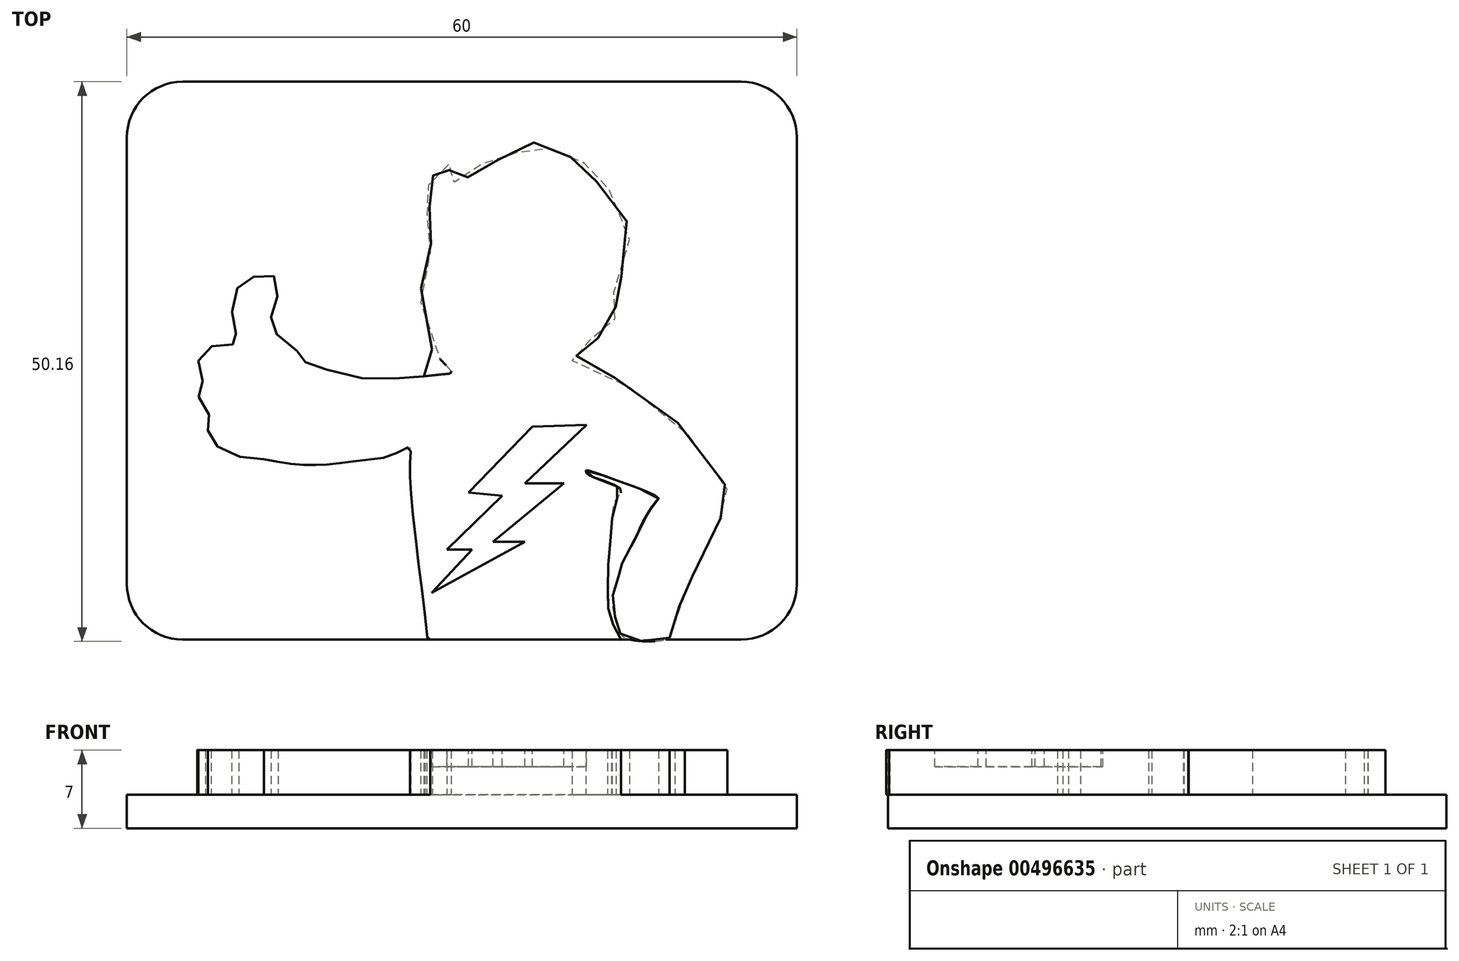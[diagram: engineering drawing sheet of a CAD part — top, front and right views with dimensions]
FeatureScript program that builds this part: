
annotation { "Feature Type Name" : "Feature", "Feature Type Description" : "" }
export const myFeature = defineFeature(function(context is Context, id is Id, definition is map)
    precondition{}
    {
        {
            var Q0;
            Q0=qCreatedBy(makeId("Top.planeOp"),FACE);
            var sketch = newSketch(context, id + "F0", { "sketchPlane" : qUnion([Q0])});
            skLineSegment(sketch, "E0", {"start": v(23.2, 0) * mm, "end": v(40.3, 0) * mm});
            skFitSpline(sketch, "E1", {"points": [v(40.3, 0) * mm, v(39.62, 1.25) * mm, v(39.17, 2.66) * mm, v(39.1, 4.54) * mm, v(39.2, 7.51) * mm, v(39.48, 10.18) * mm, v(39.82, 12.47) * mm, v(40.3, 13.43) * mm, v(37.7, 14.6) * mm, v(37.2, 14.94) * mm, v(37.16, 15.14) * mm, v(38.73, 14.7) * mm, v(43.66, 12.71) * mm, v(43.48, 12.44) * mm, v(42.15, 10.32) * mm, v(41.53, 8.95) * mm, v(40.54, 7.2) * mm, v(40.3, 6.45) * mm, v(39.96, 5.29) * mm, v(39.52, 3.2) * mm, v(40.08, 1.08) * mm, v(40.66, 0.15) * mm, v(44.65, 0.15) * mm, v(44.99, 0.8) * mm, v(45.31, 1.26) * mm, v(45.21, 2.3) * mm, v(44.8, 3.13) * mm, v(44.18, 3.06) * mm, v(43.76, 2.55) * mm, v(43.43, 2.1) * mm, v(43.67, 1.59) * mm, v(44.17, 1.67) * mm, v(44.47, 1.04) * mm, v(44.03, 0.78) * mm, v(43.09, 1.49) * mm, v(43.33, 2.68) * mm, v(43.83, 3.3) * mm, v(43.86, 3.57) * mm, v(42.44, 3.86) * mm, v(41.6, 4.26) * mm, v(41.02, 4.75) * mm, v(40.5, 5.45) * mm, v(39.97, 5.3) * mm], "startDerivative": vector(-28.08, 47.6) * mm, "endDerivative": vector(-35.62, -20.95) * mm});
            skFitSpline(sketch, "E2", {"points": [v(44.65, 0.15) * mm, v(45.37, 0.15) * mm, v(45.62, 0.84) * mm, v(46.02, 1.62) * mm, v(45.65, 2.6) * mm, v(45.25, 3.45) * mm, v(45.12, 3.62) * mm, v(45.53, 4.1) * mm, v(46.27, 4.98) * mm, v(46.55, 5.43) * mm, v(47.25, 6.7) * mm, v(48.46, 9.23) * mm, v(49.19, 10.82) * mm, v(49.4, 11.55) * mm, v(49.65, 12.38) * mm, v(49.8, 12.93) * mm, v(49.82, 13.33) * mm, v(49.73, 13.67) * mm, v(49.09, 14.73) * mm, v(47.87, 16.42) * mm, v(44.79, 20.02) * mm, v(43.5, 20.9) * mm, v(40.2, 23.17) * mm, v(38.18, 24.15) * mm, v(36.07, 24.93) * mm, v(35.93, 25.02) * mm, v(36.04, 25.17) * mm, v(36.55, 25.71) * mm, v(36.82, 26.15) * mm, v(37.2, 26.6) * mm, v(37.4, 26.83) * mm, v(37.58, 26.9) * mm, v(37.85, 26.9) * mm, v(38.4, 27.12) * mm, v(39.23, 27.62) * mm, v(39.58, 28.3) * mm, v(39.76, 28.78) * mm, v(39.86, 29.61) * mm, v(39.74, 30.08) * mm, v(39.57, 30.46) * mm, v(39.46, 30.54) * mm, v(39.48, 30.72) * mm, v(39.58, 31) * mm, v(40.1, 31.88) * mm, v(40.55, 33.5) * mm, v(41.04, 35.57) * mm, v(41.03, 36.33) * mm, v(40.66, 37.97) * mm, v(39.61, 39.82) * mm, v(38.92, 40.6) * mm, v(38.3, 40.92) * mm, v(37.92, 41.29) * mm, v(37.37, 42.14) * mm, v(37.04, 42.68) * mm, v(36.59, 43) * mm, v(36.13, 43.18) * mm, v(34.9, 43.44) * mm, v(34.07, 43.84) * mm, v(33.87, 44.16) * mm, v(33.01, 44.47) * mm, v(32.43, 44.54) * mm, v(31.55, 44.2) * mm, v(31.08, 43.7) * mm, v(30.17, 43) * mm, v(29.5, 42.98) * mm, v(28.57, 42.92) * mm, v(28.1, 42.7) * mm, v(27.57, 42.5) * mm, v(27.3, 42.14) * mm, v(26.77, 41.6) * mm, v(26, 41.02) * mm, v(25.52, 40.97) * mm, v(25, 41.04) * mm, v(24.79, 41.2) * mm, v(24.74, 41.7) * mm, v(24.91, 42.1) * mm, v(25.02, 42.42) * mm, v(25.08, 42.62) * mm, v(24.85, 42.6) * mm, v(24.47, 42.34) * mm, v(24.05, 42.15) * mm, v(23.65, 41.78) * mm, v(23.22, 41.3) * mm, v(23.11, 40.92) * mm, v(22.9, 40.4) * mm, v(22.92, 39.92) * mm, v(22.99, 39.35) * mm, v(23.17, 38.69) * mm, v(23.11, 38.44) * mm, v(22.85, 37.83) * mm, v(22.73, 37.2) * mm, v(22.86, 36.17) * mm, v(23.39, 35.2) * mm, v(23.21, 34.7) * mm, v(22.8, 33.55) * mm, v(22.57, 32.82) * mm, v(22.36, 30.77) * mm, v(22.46, 29.38) * mm, v(23.14, 26.64) * mm, v(23.7, 25.56) * mm, v(25.09, 23.95) * mm, v(24.72, 23.8) * mm, v(22.63, 23.6) * mm], "startDerivative": vector(93.7, -19.62) * mm, "endDerivative": vector(-151.22, -15.4) * mm});
            skFitSpline(sketch, "E3", {"points": [v(22.63, 23.6) * mm, v(20.3, 23.43) * mm, v(17.52, 23.37) * mm, v(14.13, 24.15) * mm, v(12.24, 24.7) * mm, v(12, 24.93) * mm, v(11.84, 25.5) * mm, v(11.2, 25.9) * mm, v(9.67, 27.12) * mm, v(9.04, 28.14) * mm, v(8.97, 28.86) * mm, v(9.36, 30.27) * mm, v(9.6, 31.24) * mm, v(9.3, 32.5) * mm, v(8.15, 32.57) * mm, v(7.2, 32.47) * mm, v(6.33, 31.92) * mm, v(5.53, 30.7) * mm, v(5.5, 29.02) * mm, v(5.68, 27.77) * mm, v(6.06, 26.81) * mm, v(5.79, 26.49) * mm, v(5.1, 26.49) * mm, v(3.73, 26.33) * mm, v(2.84, 25.61) * mm, v(2.37, 24.72) * mm, v(2.64, 23.4) * mm, v(3.08, 22.8) * mm, v(2.54, 21.87) * mm, v(2.8, 20.48) * mm, v(3.57, 20.04) * mm, v(3.43, 19.44) * mm, v(3.35, 18.24) * mm, v(3.9, 17.54) * mm, v(5, 16.75) * mm, v(6.89, 16.26) * mm, v(8.33, 16.17) * mm], "startDerivative": vector(-59.52, -4.1) * mm, "endDerivative": vector(44.84, -1) * mm});
            skFitSpline(sketch, "E4", {"points": [v(8.33, 16.17) * mm, v(10.73, 15.74) * mm, v(12.78, 15.64) * mm, v(14.55, 15.74) * mm, v(17.16, 16.08) * mm, v(19.96, 16.6) * mm, v(21.36, 17.23) * mm, v(21.43, 16.26) * mm, v(21.46, 13.46) * mm, v(22.23, 6.35) * mm, v(22.93, 0.46) * mm, v(22.96, 0.15) * mm, v(23, 0.05) * mm, v(23.2, 0) * mm], "startDerivative": vector(28.01, -5.8) * mm, "endDerivative": vector(9.43, -1.1) * mm});
            skSolve(sketch);
        }
        {
            var Q0;
            Q0 = qSketchRegion(id + "F0", true);
            extrude(context, id + "F1", {"entities" : qUnion([Q0]), "depth" : 4 * mm, "offsetDistance" : 25 * mm});
        }
        {
            var Q0;
            Q0=qCreatedBy(makeId("Top.planeOp"),FACE);
            var sketch = newSketch(context, id + "F2", { "sketchPlane" : qUnion([Q0])});
            skLineSegment(sketch, "E5.bottom", {"start": v(1.05, 50) * mm, "end": v(51.05, 50) * mm});
            skLineSegment(sketch, "E5.top", {"start": v(1.05, 0) * mm, "end": v(51.05, 0) * mm});
            skLineSegment(sketch, "E5.left", {"start": v(-3.95, 45) * mm, "end": v(-3.95, 5) * mm});
            skLineSegment(sketch, "E5.right", {"start": v(56.05, 45) * mm, "end": v(56.05, 5) * mm});
            skPoint(sketch, "E6.visualSharp", {"position": v(-3.95, 50) * mm});
            skArc(sketch, "E6.filletArc", {"start": v(1.05, 50) * mm, "mid": v(-2.49, 48.54) * mm, "end": v(-3.95, 45) * mm});
            skPoint(sketch, "E7.visualSharp", {"position": v(56.05, 50) * mm});
            skArc(sketch, "E7.filletArc", {"start": v(56.05, 45) * mm, "mid": v(54.58, 48.54) * mm, "end": v(51.05, 50) * mm});
            skPoint(sketch, "E8.visualSharp", {"position": v(56.05, 0) * mm});
            skArc(sketch, "E8.filletArc", {"start": v(51.05, 0) * mm, "mid": v(54.58, 1.46) * mm, "end": v(56.05, 5) * mm});
            skPoint(sketch, "E9.visualSharp", {"position": v(-3.95, 0) * mm});
            skArc(sketch, "E9.filletArc", {"start": v(-3.95, 5) * mm, "mid": v(-2.49, 1.46) * mm, "end": v(1.05, 0) * mm});
            skSolve(sketch);
        }
        {
            var Q0;
            Q0 = qSketchRegion(id + "F2", true);
            extrude(context, id + "F3", {"entities" : qUnion([Q0]), "operationType" : NewBodyOperationType.ADD, "oppositeDirection" : true, "depth" : 3 * mm, "offsetDistance" : 25 * mm});
        }
        {
            var Q0;
            Q0=makeQuery(id+"F1.opExtrude","CAP_FACE",FACE,{"disambiguationData":[OSD([sQuery(id+"F0.wireOp",EDGE,"E0"),sQuery(id+"F0.wireOp",EDGE,"E1"),sQuery(id+"F0.wireOp",EDGE,"E2"),sQuery(id+"F0.wireOp",EDGE,"E3"),sQuery(id+"F0.wireOp",EDGE,"E4")])],"isStart":false});
            var sketch = newSketch(context, id + "F4", { "sketchPlane" : qUnion([Q0])});
            skLineSegment(sketch, "E10", {"start": v(32.37, 19.07) * mm, "end": v(26.63, 13.17) * mm});
            skLineSegment(sketch, "E11", {"start": v(26.63, 13.17) * mm, "end": v(29.67, 12.9) * mm});
            skLineSegment(sketch, "E12", {"start": v(29.67, 12.9) * mm, "end": v(24.7, 8.07) * mm});
            skLineSegment(sketch, "E13", {"start": v(24.7, 8.07) * mm, "end": v(26.97, 8.07) * mm});
            skLineSegment(sketch, "E14", {"start": v(26.97, 8.07) * mm, "end": v(23.34, 4.18) * mm});
            skLineSegment(sketch, "E15", {"start": v(23.34, 4.18) * mm, "end": v(31.69, 8.77) * mm});
            skLineSegment(sketch, "E16", {"start": v(31.69, 8.77) * mm, "end": v(28.83, 8.77) * mm});
            skLineSegment(sketch, "E17", {"start": v(28.83, 8.77) * mm, "end": v(35.17, 14) * mm});
            skLineSegment(sketch, "E18", {"start": v(35.17, 14) * mm, "end": v(31.69, 14) * mm});
            skLineSegment(sketch, "E19", {"start": v(31.69, 14) * mm, "end": v(37.21, 19.24) * mm});
            skLineSegment(sketch, "E20", {"start": v(37.21, 19.24) * mm, "end": v(32.37, 19.07) * mm});
            skSolve(sketch);
        }
        {
            var Q0;
            Q0 = qSketchRegion(id + "F4", true);
            var Q1;
            {var subQ0=sQuery(id+"F2.wireOp",EDGE,"E5.right");var subQ1=sQuery(id+"F0.wireOp",EDGE,"E4");var subQ2=sQuery(id+"F2.wireOp",EDGE,"E5.left");var subQ3=sQuery(id+"F0.wireOp",EDGE,"E3");var subQ4=sQuery(id+"F0.wireOp",EDGE,"E0");var subQ5=sQuery(id+"F2.wireOp",EDGE,"E5.bottom");var subQ6=sQuery(id+"F0.wireOp",EDGE,"E2");var subQ7=sQuery(id+"F0.wireOp",EDGE,"E1");var subQ8=sQuery(id+"F2.wireOp",EDGE,"E5.top");var subQ9=sQuery(id+"F2.wireOp",EDGE,"E6.filletArc");var subQ10=sQuery(id+"F2.wireOp",EDGE,"E7.filletArc");var subQ11=sQuery(id+"F2.wireOp",EDGE,"E8.filletArc");var subQ12=sQuery(id+"F2.wireOp",EDGE,"E9.filletArc");Q1=makeQuery(id+"F3.boolean.opBoolean","SPLIT",FACE,{"disambiguationData":[TD([makeQuery(id+"F1.opExtrude","SWEPT_FACE",FACE,{"disambiguationData":[OSD([subQ4])]}),makeQuery(id+"F1.opExtrude","CAP_FACE",FACE,{"disambiguationData":[OSD([subQ4,subQ7,subQ6,subQ3,subQ1])],"isStart":true}),makeQuery(id+"F1.opExtrude","SWEPT_FACE",FACE,{"disambiguationData":[OSD([subQ7])]}),makeQuery(id+"F1.opExtrude","SWEPT_FACE",FACE,{"disambiguationData":[OSD([subQ6])]}),makeQuery(id+"F1.opExtrude","SWEPT_FACE",FACE,{"disambiguationData":[OSD([subQ3])]}),makeQuery(id+"F1.opExtrude","SWEPT_FACE",FACE,{"disambiguationData":[OSD([subQ1])]}),makeQuery(id+"F3.opExtrude","SWEPT_FACE",FACE,{"disambiguationData":[OSD([subQ5])]}),makeQuery(id+"F3.opExtrude","SWEPT_FACE",FACE,{"disambiguationData":[OSD([subQ8])]}),makeQuery(id+"F3.opExtrude","SWEPT_FACE",FACE,{"disambiguationData":[OSD([subQ2])]}),makeQuery(id+"F3.opExtrude","SWEPT_FACE",FACE,{"disambiguationData":[OSD([subQ0])]}),makeQuery(id+"F3.opExtrude","SWEPT_FACE",FACE,{"disambiguationData":[OSD([subQ9])]}),makeQuery(id+"F3.opExtrude","SWEPT_FACE",FACE,{"disambiguationData":[OSD([subQ10])]}),makeQuery(id+"F3.opExtrude","SWEPT_FACE",FACE,{"disambiguationData":[OSD([subQ11])]}),makeQuery(id+"F3.opExtrude","SWEPT_FACE",FACE,{"disambiguationData":[OSD([subQ12])]})])],"derivedFrom":makeQuery(id+"F3.opExtrude","CAP_FACE",FACE,{"disambiguationData":[OSD([subQ5,subQ8,subQ2,subQ0,subQ9,subQ10,subQ11,subQ12])],"isStart":true})});}
            var Q2;
            Q2=makeQuery(id+"F1.opExtrude","SWEPT_BODY",BODY,{"disambiguationData":[OSD([sQuery(id+"F0.wireOp",EDGE,"E0"),sQuery(id+"F0.wireOp",EDGE,"E1"),sQuery(id+"F0.wireOp",EDGE,"E2"),sQuery(id+"F0.wireOp",EDGE,"E3"),sQuery(id+"F0.wireOp",EDGE,"E4")])]});
            extrude(context, id + "F5", {"entities" : qUnion([Q0]), "operationType" : NewBodyOperationType.REMOVE, "oppositeDirection" : true, "depth" : 1.5 * mm, "endBoundEntityFace" : qUnion([Q1]), "endBoundEntityBody" : qUnion([Q2]), "offsetDistance" : 25 * mm});
        }
    });
